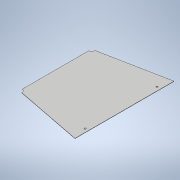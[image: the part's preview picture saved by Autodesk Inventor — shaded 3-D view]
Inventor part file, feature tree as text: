
AUTODESK INVENTOR PART (.ipt)
format: ipt  version: 2021 (Build 250183000, 183)  size: 128,000 bytes
history: native  units: in
note: dims shown in document units (in); Inventor stores cm internally (conversion verified against a paired STEP export)
features: extrude x2, sketch x1
ambient origin geometry x8: Origin, YZ Plane, XZ Plane, XY Plane, X Axis, Y Axis, Z Axis, Center Point
bodies: Solid1 (feature_tree)
feature tree (3):
  extrude  "Extrusion1"  Depth=11.0in
  extrude  "Extrusion2"  Depth=11.0in
  sketch  "Sketch2"  dims[d12=15.325in d13=11.0in d14=11.0in d15=8.0in d16=8.0in d17=0.06in d18=0.0in d23=1.25in d24=1.25in d26=5.1in d29=8.0in d30=0.75in d31=0.375in d32=8.0in d33=0.75in d34=0.375in d35=8.0in d36=0.75in d37=8.0in d38=0.75in d41=1.0in d42=0.0in]
